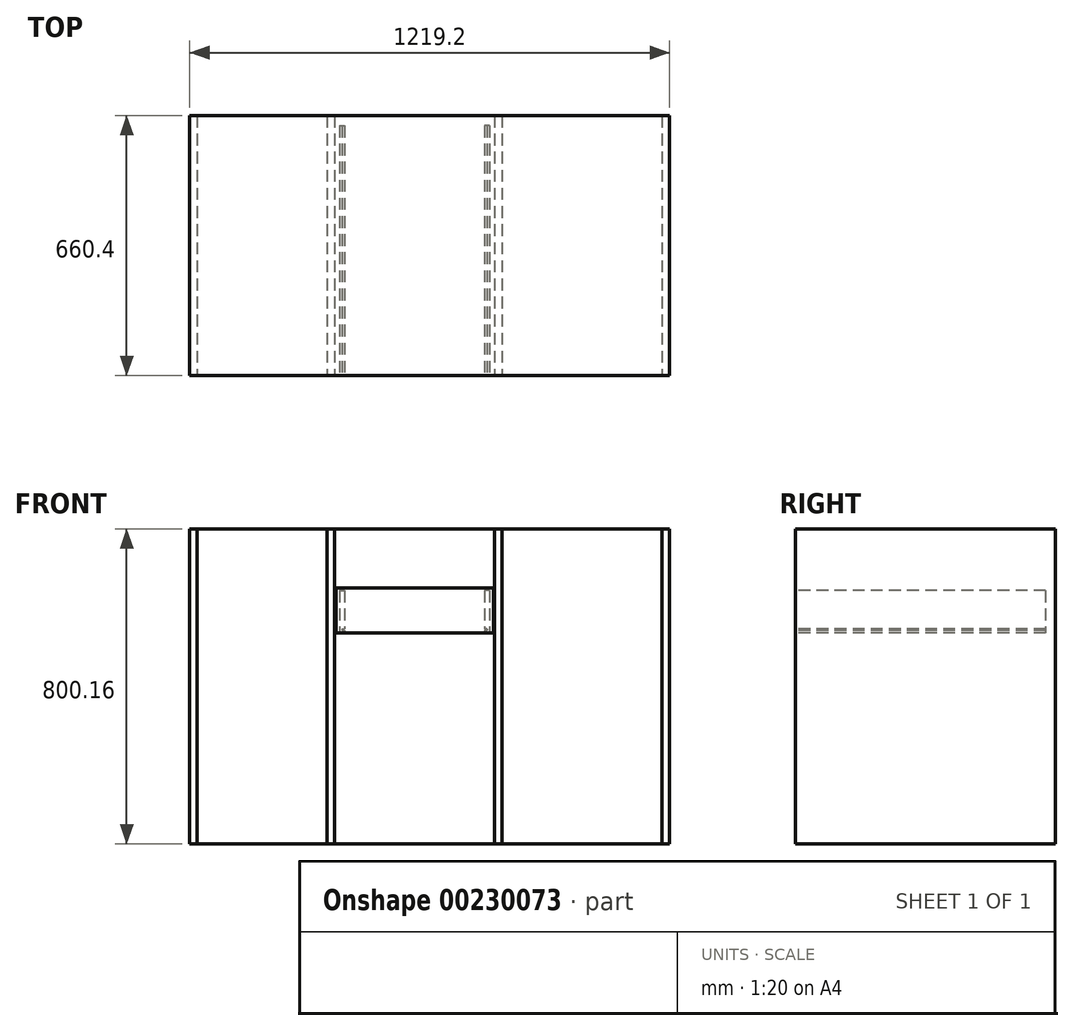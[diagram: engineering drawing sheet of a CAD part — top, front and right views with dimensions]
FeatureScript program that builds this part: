
annotation { "Feature Type Name" : "Feature", "Feature Type Description" : "" }
export const myFeature = defineFeature(function(context is Context, id is Id, definition is map)
    precondition{}
    {
        {
            var Q0;
            Q0=qCreatedBy(makeId("Top.planeOp"),FACE);
            var sketch = newSketch(context, id + "F0", { "sketchPlane" : qUnion([Q0])});
            skLineSegment(sketch, "E0.bottom", {"start": v(-604.04, -289.26) * mm, "end": v(615.16, -289.26) * mm});
            skLineSegment(sketch, "E0.top", {"start": v(-604.04, 371.14) * mm, "end": v(615.16, 371.14) * mm});
            skLineSegment(sketch, "E0.left", {"start": v(-604.04, -289.26) * mm, "end": v(-604.04, 371.14) * mm});
            skLineSegment(sketch, "E0.right", {"start": v(615.16, -289.26) * mm, "end": v(615.16, 371.14) * mm});
            skSolve(sketch);
        }
        {
            var Q0;
            Q0 = qSketchRegion(id + "F0", true);
            extrude(context, id + "F1", {"entities" : qUnion([Q0]), "depth" : 3 / 101.6 * mm});
        }
        {
            var Q0;
            Q0=makeQuery(id+"F1.opExtrude","CAP_FACE",FACE,{"disambiguationData":[OSD([sQuery(id+"F0.wireOp",EDGE,"E0.bottom"),sQuery(id+"F0.wireOp",EDGE,"E0.top"),sQuery(id+"F0.wireOp",EDGE,"E0.left"),sQuery(id+"F0.wireOp",EDGE,"E0.right")])],"isStart":true});
            var sketch = newSketch(context, id + "F2", { "sketchPlane" : qUnion([Q0])});
            skLineSegment(sketch, "E1.bottom", {"start": v(-604.04, -371.14) * mm, "end": v(-584.99, -371.14) * mm});
            skLineSegment(sketch, "E1.top", {"start": v(-604.04, 289.26) * mm, "end": v(-584.99, 289.26) * mm});
            skLineSegment(sketch, "E1.left", {"start": v(-604.04, -371.14) * mm, "end": v(-604.04, 289.26) * mm});
            skLineSegment(sketch, "E1.right", {"start": v(-584.99, -371.14) * mm, "end": v(-584.99, 289.26) * mm});
            skLineSegment(sketch, "E2.bottom", {"start": v(615.16, -371.14) * mm, "end": v(596.11, -371.14) * mm});
            skLineSegment(sketch, "E2.top", {"start": v(615.16, 289.26) * mm, "end": v(596.11, 289.26) * mm});
            skLineSegment(sketch, "E2.left", {"start": v(615.16, -371.14) * mm, "end": v(615.16, 289.26) * mm});
            skLineSegment(sketch, "E2.right", {"start": v(596.11, -371.14) * mm, "end": v(596.11, 289.26) * mm});
            skLineSegment(sketch, "E3.bottom", {"start": v(170.66, -371.14) * mm, "end": v(189.71, -371.14) * mm});
            skLineSegment(sketch, "E3.top", {"start": v(170.66, 289.26) * mm, "end": v(189.71, 289.26) * mm});
            skLineSegment(sketch, "E3.left", {"start": v(170.66, -371.14) * mm, "end": v(170.66, 289.26) * mm});
            skLineSegment(sketch, "E3.right", {"start": v(189.71, -371.14) * mm, "end": v(189.71, 289.26) * mm});
            skLineSegment(sketch, "E4.bottom", {"start": v(-254.79, -371.14) * mm, "end": v(-235.74, -371.14) * mm});
            skLineSegment(sketch, "E4.top", {"start": v(-254.79, 289.26) * mm, "end": v(-235.74, 289.26) * mm});
            skLineSegment(sketch, "E4.left", {"start": v(-254.79, -371.14) * mm, "end": v(-254.79, 289.26) * mm});
            skLineSegment(sketch, "E4.right", {"start": v(-235.74, -371.14) * mm, "end": v(-235.74, 289.26) * mm});
            skSolve(sketch);
        }
        {
            var Q0;
            Q0 = qSketchRegion(id + "F2", true);
            extrude(context, id + "F3", {"entities" : qUnion([Q0]), "depth" : 800.1 * mm});
        }
        {
            var Q0;
            Q0=makeQuery(id+"F3.opExtrude","CAP_FACE",FACE,{"disambiguationData":[OSD([sQuery(id+"F2.wireOp",EDGE,"E1.bottom"),sQuery(id+"F2.wireOp",EDGE,"E1.top"),sQuery(id+"F2.wireOp",EDGE,"E1.left"),sQuery(id+"F2.wireOp",EDGE,"E1.right")])],"isStart":false});
            var sketch = newSketch(context, id + "F4", { "sketchPlane" : qUnion([Q0])});
            skLineSegment(sketch, "E5.bottom", {"start": v(-604.04, -371.14) * mm, "end": v(615.16, -371.14) * mm});
            skLineSegment(sketch, "E5.top", {"start": v(-604.04, 289.26) * mm, "end": v(615.16, 289.26) * mm});
            skLineSegment(sketch, "E5.left", {"start": v(-604.04, -371.14) * mm, "end": v(-604.04, 289.26) * mm});
            skLineSegment(sketch, "E5.right", {"start": v(615.16, -371.14) * mm, "end": v(615.16, 289.26) * mm});
            skSolve(sketch);
        }
        {
            var Q0;
            Q0 = qSketchRegion(id + "F4", true);
            extrude(context, id + "F5", {"entities" : qUnion([Q0]), "depth" : 3 / 101.6 * mm});
        }
        {
            var Q0;
            Q0=makeQuery(id+"F5.boolean.opBoolean","MERGE",FACE,{"derivedFrom":[makeQuery(id+"F3.boolean.opBoolean","MERGE",FACE,{"derivedFrom":[makeQuery(id+"F1.opExtrude","SWEPT_FACE",FACE,{"disambiguationData":[OSD([sQuery(id+"F0.wireOp",EDGE,"E0.bottom")])]}),makeQuery(id+"F3.opExtrude","SWEPT_FACE",FACE,{"disambiguationData":[OSD([sQuery(id+"F2.wireOp",EDGE,"E1.top")])]}),makeQuery(id+"F3.opExtrude","SWEPT_FACE",FACE,{"disambiguationData":[OSD([sQuery(id+"F2.wireOp",EDGE,"E2.top")])]}),makeQuery(id+"F3.opExtrude","SWEPT_FACE",FACE,{"disambiguationData":[OSD([sQuery(id+"F2.wireOp",EDGE,"E3.top")])]}),makeQuery(id+"F3.opExtrude","SWEPT_FACE",FACE,{"disambiguationData":[OSD([sQuery(id+"F2.wireOp",EDGE,"E4.top")])]})]}),makeQuery(id+"F5.opExtrude","SWEPT_FACE",FACE,{"disambiguationData":[OSD([sQuery(id+"F4.wireOp",EDGE,"E5.top")])]})]});
            var sketch = newSketch(context, id + "F6", { "sketchPlane" : qUnion([Q0])});
            skLineSegment(sketch, "E6.bottom", {"start": v(-232.56, -149.69) * mm, "end": v(167.49, -149.69) * mm});
            skLineSegment(sketch, "E6.top", {"start": v(-232.56, -263.99) * mm, "end": v(167.49, -263.99) * mm});
            skLineSegment(sketch, "E6.left", {"start": v(-232.56, -149.69) * mm, "end": v(-232.56, -263.99) * mm});
            skLineSegment(sketch, "E6.right", {"start": v(167.49, -149.69) * mm, "end": v(167.49, -263.99) * mm});
            skSolve(sketch);
        }
        {
            var Q0;
            Q0 = qSketchRegion(id + "F6", true);
            extrude(context, id + "F7", {"entities" : qUnion([Q0]), "oppositeDirection" : true, "depth" : 3 / 101.6 * mm});
        }
        {
            var Q0;
            Q0=makeQuery(id+"F7.opExtrude","CAP_FACE",FACE,{"disambiguationData":[OSD([sQuery(id+"F6.wireOp",EDGE,"E6.bottom"),sQuery(id+"F6.wireOp",EDGE,"E6.top"),sQuery(id+"F6.wireOp",EDGE,"E6.left"),sQuery(id+"F6.wireOp",EDGE,"E6.right")])],"isStart":false});
            var sketch = newSketch(context, id + "F8", { "sketchPlane" : qUnion([Q0])});
            skLineSegment(sketch, "E7.bottom", {"start": v(-157.96, -156.04) * mm, "end": v(-145.26, -156.04) * mm});
            skLineSegment(sketch, "E7.top", {"start": v(-157.96, -263.99) * mm, "end": v(-145.26, -263.99) * mm});
            skLineSegment(sketch, "E7.left", {"start": v(-157.96, -156.04) * mm, "end": v(-157.96, -263.99) * mm});
            skLineSegment(sketch, "E7.right", {"start": v(-145.26, -156.04) * mm, "end": v(-145.26, -253.67) * mm});
            skLineSegment(sketch, "E8.bottom", {"start": v(-151.61, -253.67) * mm, "end": v(-145.26, -253.67) * mm});
            skLineSegment(sketch, "E8.top", {"start": v(-151.61, -257.64) * mm, "end": v(-145.26, -257.64) * mm});
            skLineSegment(sketch, "E8.left", {"start": v(-151.61, -253.67) * mm, "end": v(-151.61, -257.64) * mm});
            skLineSegment(sketch, "E9.trimOffspring", {"start": v(-145.26, -257.64) * mm, "end": v(-145.26, -263.99) * mm});
            skLineSegment(sketch, "E10", {"start": v(32.54, -0.04) * mm, "end": v(32.54, -299.34) * mm, "construction": true});
            skLineSegment(sketch, "E11.MirrorCS", {"start": v(216.69, -257.64) * mm, "end": v(210.34, -257.64) * mm});
            skLineSegment(sketch, "E12.MirrorCS", {"start": v(216.69, -253.67) * mm, "end": v(216.69, -257.64) * mm});
            skLineSegment(sketch, "E13.MirrorCS", {"start": v(216.69, -253.67) * mm, "end": v(210.34, -253.67) * mm});
            skLineSegment(sketch, "E14.MirrorCS", {"start": v(210.34, -257.64) * mm, "end": v(210.34, -263.99) * mm});
            skLineSegment(sketch, "E15.MirrorCS", {"start": v(223.04, -263.99) * mm, "end": v(210.34, -263.99) * mm});
            skLineSegment(sketch, "E16.MirrorCS", {"start": v(210.34, -156.04) * mm, "end": v(210.34, -253.67) * mm});
            skLineSegment(sketch, "E17.MirrorCS", {"start": v(223.04, -156.04) * mm, "end": v(223.04, -263.99) * mm});
            skLineSegment(sketch, "E18.MirrorCS", {"start": v(223.04, -156.04) * mm, "end": v(210.34, -156.04) * mm});
            skSolve(sketch);
        }
        {
            var Q0;
            Q0 = qSketchRegion(id + "F8", true);
            extrude(context, id + "F9", {"entities" : qUnion([Q0]), "depth" : 635 * mm});
        }
    });
